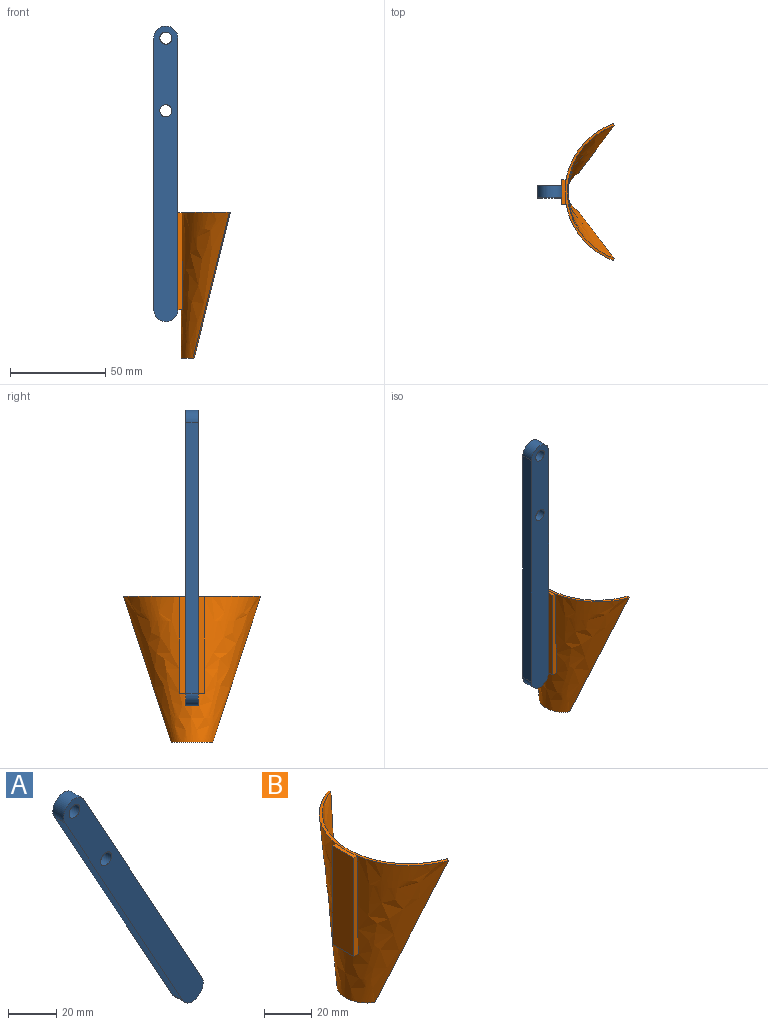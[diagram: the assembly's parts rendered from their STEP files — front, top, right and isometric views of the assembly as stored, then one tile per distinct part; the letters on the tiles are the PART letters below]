
ASSEMBLY  parts=2 mates=1
PART A: 8 faces, bbox 81.6x6.4x137.1 mm
  f0: plane 124.42x68.93mm, normal (-0.87,0,-0.48), area 903.2mm2, adj f1,f5,f6,f7
  f1: cylinder r=6.35mm len=11.9mm, axis (0,1,0), area 126.7mm2, adj f0,f2,f6,f7
  f2: plane 124.42x68.93mm, normal (0.87,0,0.48), area 903.2mm2, adj f1,f5,f6,f7
  f3: cylinder r=3.17mm len=6.35mm, axis (0,1,0), area 126.7mm2, adj f6,f7
  f4: cylinder r=3.17mm len=6.35mm, axis (0,1,0), area 126.7mm2, adj f6,f7
  f5: cylinder r=6.35mm len=11.9mm, axis (0,1,0), area 126.7mm2, adj f0,f2,f6,f7
  f6: plane 137.12x81.63mm, normal (0,-1,0), area 1869.8mm2, adj f0,f1,f2,f3,f4,f5
  f7: plane 137.12x81.63mm, normal (0,1,0), area 1869.8mm2, adj f0,f1,f2,f3,f4,f5
PART B: 11 faces, bbox 29.9x74.4x79 mm
  f0: bspline ~76.48x26.01mm, area 104.7mm2, adj f1,f3,f4,f5
  f1: bspline ~71.84x25.8mm, area 117.2mm2, adj f0,f2,f4,f5,f8
  f2: bspline ~76.48x26.01mm, area 104.7mm2, adj f1,f3,f4,f5
  f3: bspline ~22x6.98mm, area 32.1mm2, adj f0,f2,f4,f5
  f4: offset ~78.74x74.38mm, area 4369.6mm2, adj f0,f1,f2,f3
  f5: bspline ~76.2x71.84mm, area 3955mm2, adj f0,f1,f2,f3,f6,f7,f9
  f6: plane 50.8x2.57mm, normal (0,-1,0), area 116.8mm2, adj f5,f8,f9,f10
  f7: plane 50.8x2.57mm, normal (0,1,0), area 116.8mm2, adj f5,f8,f9,f10
  f8: plane 12.71x2.13mm, normal (0,0,1), area 22.4mm2, adj f1,f6,f7,f10
  f9: plane 12.7x2.57mm, normal (0,0,-1), area 24.3mm2, adj f5,f6,f7,f10
  f10: plane 50.8x12.7mm, normal (-1,0,0), area 645.2mm2, adj f6,f7,f8,f9
PLACE A rot(axis=(0,1,0),29deg) t=(92.5,0,5.28)mm
PLACE B t=(1.59,0,-91.44)mm
MATE fastened B.f10 <-> A.f2  axis (-1,0,0) through (0,0,-142.24)mm
